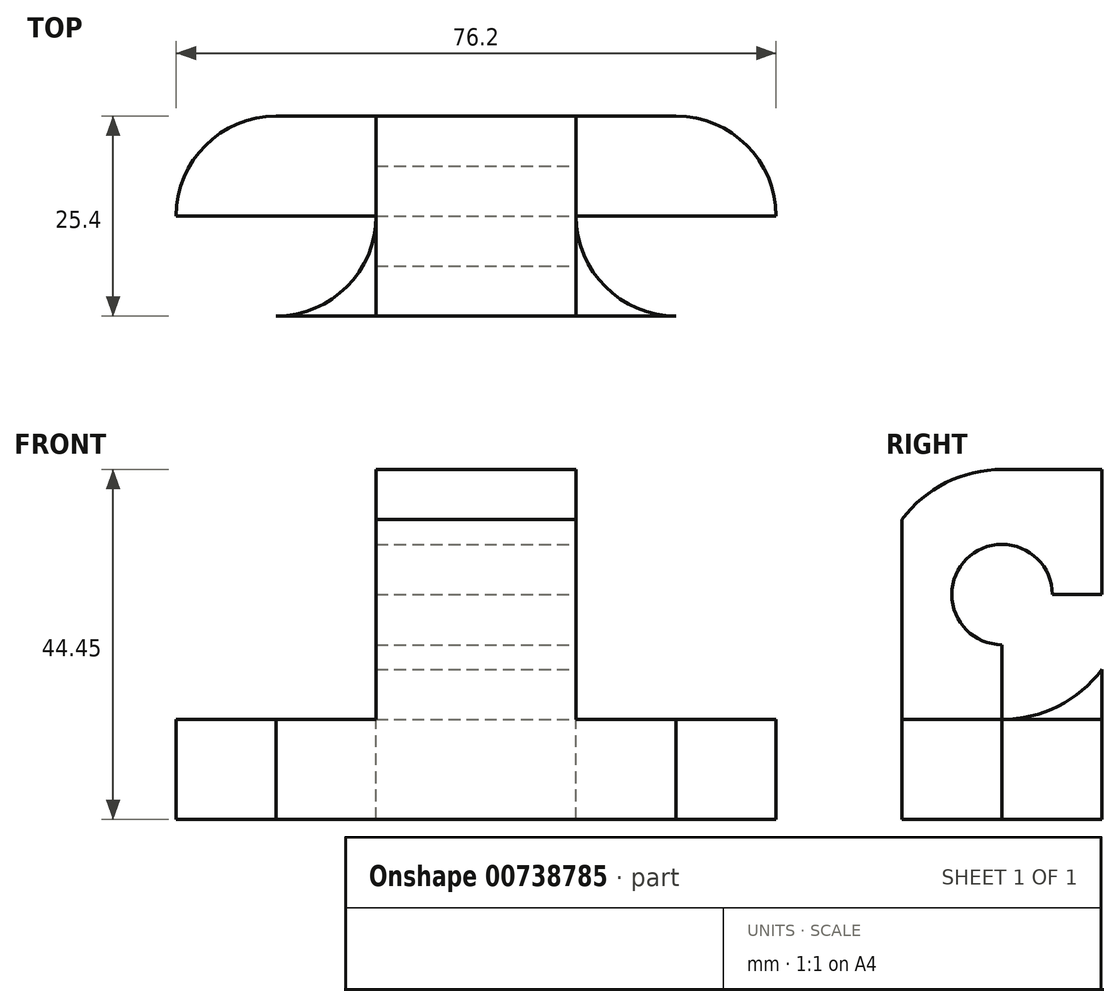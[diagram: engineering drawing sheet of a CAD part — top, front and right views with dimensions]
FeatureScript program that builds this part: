
annotation { "Feature Type Name" : "Feature", "Feature Type Description" : "" }
export const myFeature = defineFeature(function(context is Context, id is Id, definition is map)
    precondition{}
    {
        {
            var Q0;
            Q0=qCreatedBy(makeId("Front.planeOp"),FACE);
            var sketch = newSketch(context, id + "F0", { "sketchPlane" : qUnion([Q0])});
            skLineSegment(sketch, "E0", {"start": v(-25.4, 0) * mm, "end": v(-25.4, 12.7) * mm});
            skLineSegment(sketch, "E1", {"start": v(-25.4, 12.7) * mm, "end": v(0, 12.7) * mm});
            skLineSegment(sketch, "E2", {"start": v(0, 12.7) * mm, "end": v(0, 44.45) * mm});
            skLineSegment(sketch, "E3", {"start": v(0, 44.45) * mm, "end": v(25.4, 44.45) * mm});
            skLineSegment(sketch, "E4", {"start": v(25.4, 44.45) * mm, "end": v(25.4, 12.7) * mm});
            skLineSegment(sketch, "E5", {"start": v(25.4, 12.7) * mm, "end": v(50.8, 12.7) * mm});
            skLineSegment(sketch, "E6", {"start": v(50.8, 12.7) * mm, "end": v(50.8, 0) * mm});
            skLineSegment(sketch, "E7", {"start": v(50.8, 0) * mm, "end": v(-25.4, 0) * mm});
            skSolve(sketch);
        }
        {
            var Q0;
            Q0 = qSketchRegion(id + "F0", true);
            extrude(context, id + "F1", {"entities" : qUnion([Q0]), "depth" : 25.4 * mm, "offsetDistance" : 25.4 * mm});
        }
        {
            var Q0;
            Q0=makeQuery(id+"F1.opExtrude","SWEPT_FACE",FACE,{"disambiguationData":[OSD([sQuery(id+"F0.wireOp",EDGE,"E4")])]});
            var sketch = newSketch(context, id + "F2", { "sketchPlane" : qUnion([Q0])});
            skLineSegment(sketch, "E8", {"start": v(-12.7, 44.45) * mm, "end": v(-12.7, 12.7) * mm});
            skLineSegment(sketch, "E9", {"start": v(-25.4, 28.57) * mm, "end": v(0, 28.57) * mm});
            skCircle(sketch, "E10", {"center": v(-12.7, 28.57) * mm, "radius": 6.38 * mm});
            skCircle(sketch, "E11", {"center": v(-12.7, 28.57) * mm, "radius": 15.88 * mm});
            skSolve(sketch);
        }
        {
            var Q0;
            {var subQ0=sQuery(id+"F2.wireOp",EDGE,"E11");var subQ1=makeQuery(id+"F1.opExtrude","CAP_EDGE",EDGE,{"disambiguationData":[OSD([sQuery(id+"F0.wireOp",EDGE,"E4")])],"isStart":false});var subQ2=makeQuery(id+"F2.imprint","INTERSECT",VERTEX,{"disambiguationData":[OD(0.0)],"derivedFrom":[subQ1,subQ0]});Q0=makeQuery(id+"F2.imprint","IMPRINT",FACE,{"disambiguationData":[TD([[makeQuery(id+"F2.imprint","IMPRINT",EDGE,{"disambiguationData":[TD([[subQ2,-1.0]])],"derivedFrom":subQ0}),1.0]])]});}
            var Q1;
            {var subQ0=sQuery(id+"F2.wireOp",EDGE,"E11");var subQ1=makeQuery(id+"F1.opExtrude","CAP_EDGE",EDGE,{"disambiguationData":[OSD([sQuery(id+"F0.wireOp",EDGE,"E4")])],"isStart":true});var subQ2=makeQuery(id+"F2.imprint","INTERSECT",VERTEX,{"disambiguationData":[OD(0.0)],"derivedFrom":[subQ1,subQ0]});Q1=makeQuery(id+"F2.imprint","IMPRINT",FACE,{"disambiguationData":[TD([[makeQuery(id+"F2.imprint","IMPRINT",EDGE,{"disambiguationData":[TD([[subQ2,1.0]])],"derivedFrom":subQ0}),1.0]])]});}
            var Q2;
            {var subQ0=sQuery(id+"F2.wireOp",EDGE,"E11");var subQ1=sQuery(id+"F0.wireOp",EDGE,"E4");var subQ4=makeQuery(id+"F1.opExtrude","CAP_EDGE",EDGE,{"disambiguationData":[OSD([subQ1])],"isStart":true});var subQ5=makeQuery(id+"F2.imprint","INTERSECT",VERTEX,{"disambiguationData":[OD(0.0)],"derivedFrom":[subQ4,subQ0]});Q2=makeQuery(id+"F2.imprint","IMPRINT",FACE,{"disambiguationData":[TD([[makeQuery(id+"F2.imprint","IMPRINT",EDGE,{"disambiguationData":[TD([[subQ5,1.0]])],"derivedFrom":subQ4}),-1.0]])]});}
            var Q3;
            {var subQ0=sQuery(id+"F2.wireOp",EDGE,"E11");var subQ1=sQuery(id+"F0.wireOp",EDGE,"E4");var subQ4=makeQuery(id+"F1.opExtrude","CAP_EDGE",EDGE,{"disambiguationData":[OSD([subQ1])],"isStart":false});var subQ5=makeQuery(id+"F2.imprint","INTERSECT",VERTEX,{"disambiguationData":[OD(0.0)],"derivedFrom":[subQ4,subQ0]});Q3=makeQuery(id+"F2.imprint","IMPRINT",FACE,{"disambiguationData":[TD([[makeQuery(id+"F2.imprint","IMPRINT",EDGE,{"disambiguationData":[TD([[subQ5,1.0]])],"derivedFrom":subQ4}),1.0]])]});}
            var Q4;
            {var subQ0=sQuery(id+"F2.wireOp",EDGE,"E10");var subQ1=sQuery(id+"F2.wireOp",EDGE,"E8");var subQ2=makeQuery(id+"F2.imprint","INTERSECT",VERTEX,{"disambiguationData":[OD(0.0)],"derivedFrom":[subQ1,subQ0]});Q4=makeQuery(id+"F2.imprint","IMPRINT",FACE,{"disambiguationData":[TD([[makeQuery(id+"F2.imprint","IMPRINT",EDGE,{"disambiguationData":[TD([[subQ2,-1.0]])],"derivedFrom":subQ1}),1.0]])]});}
            var Q5;
            {var subQ0=sQuery(id+"F2.wireOp",EDGE,"E10");var subQ1=sQuery(id+"F2.wireOp",EDGE,"E8");var subQ2=makeQuery(id+"F2.imprint","INTERSECT",VERTEX,{"disambiguationData":[OD(0.0)],"derivedFrom":[subQ1,subQ0]});Q5=makeQuery(id+"F2.imprint","IMPRINT",FACE,{"disambiguationData":[TD([[makeQuery(id+"F2.imprint","IMPRINT",EDGE,{"disambiguationData":[TD([[subQ2,-1.0]])],"derivedFrom":subQ1}),-1.0]])]});}
            var Q6;
            {var subQ0=sQuery(id+"F2.wireOp",EDGE,"E9");var subQ1=sQuery(id+"F2.wireOp",EDGE,"E8");var subQ2=makeQuery(id+"F2.imprint","INTERSECT",VERTEX,{"derivedFrom":[subQ1,subQ0]});Q6=makeQuery(id+"F2.imprint","IMPRINT",FACE,{"disambiguationData":[TD([[makeQuery(id+"F2.imprint","IMPRINT",EDGE,{"disambiguationData":[TD([[subQ2,-1.0]])],"derivedFrom":subQ1}),1.0]])]});}
            var Q7;
            {var subQ0=sQuery(id+"F2.wireOp",EDGE,"E9");var subQ1=sQuery(id+"F2.wireOp",EDGE,"E8");var subQ2=makeQuery(id+"F2.imprint","INTERSECT",VERTEX,{"derivedFrom":[subQ1,subQ0]});Q7=makeQuery(id+"F2.imprint","IMPRINT",FACE,{"disambiguationData":[TD([[makeQuery(id+"F2.imprint","IMPRINT",EDGE,{"disambiguationData":[TD([[subQ2,-1.0]])],"derivedFrom":subQ1}),-1.0]])]});}
            extrude(context, id + "F3", {"entities" : qUnion([Q0, Q1, Q2, Q3, Q4, Q5, Q6, Q7]), "operationType" : NewBodyOperationType.REMOVE, "oppositeDirection" : true, "depth" : 25.4 * mm, "offsetDistance" : 25.4 * mm});
        }
        {
            var Q0;
            Q0=makeQuery(id+"F1.opExtrude","SWEPT_FACE",FACE,{"disambiguationData":[OSD([sQuery(id+"F0.wireOp",EDGE,"E5")])]});
            var sketch = newSketch(context, id + "F4", { "sketchPlane" : qUnion([Q0])});
            skLineSegment(sketch, "E12", {"start": v(38.1, 0) * mm, "end": v(38.1, -25.4) * mm});
            skLineSegment(sketch, "E13", {"start": v(50.8, -12.7) * mm, "end": v(25.4, -12.7) * mm});
            skCircle(sketch, "E14", {"center": v(38.1, -12.7) * mm, "radius": 6.35 * mm});
            skCircle(sketch, "E15", {"center": v(38.1, -12.7) * mm, "radius": 12.7 * mm});
            skSolve(sketch);
        }
        {
            var Q0;
            {var subQ0=sQuery(id+"F4.wireOp",EDGE,"E13");var subQ1=sQuery(id+"F4.wireOp",EDGE,"E12");var subQ2=makeQuery(id+"F4.imprint","INTERSECT",VERTEX,{"derivedFrom":[subQ1,subQ0]});Q0=makeQuery(id+"F4.imprint","IMPRINT",FACE,{"disambiguationData":[TD([[makeQuery(id+"F4.imprint","IMPRINT",EDGE,{"disambiguationData":[TD([[subQ2,-1.0]])],"derivedFrom":subQ1}),1.0]])]});}
            var Q1;
            {var subQ0=sQuery(id+"F4.wireOp",EDGE,"E14");var subQ1=sQuery(id+"F4.wireOp",EDGE,"E12");var subQ2=makeQuery(id+"F4.imprint","INTERSECT",VERTEX,{"disambiguationData":[OD(0.0)],"derivedFrom":[subQ1,subQ0]});Q1=makeQuery(id+"F4.imprint","IMPRINT",FACE,{"disambiguationData":[TD([[makeQuery(id+"F4.imprint","IMPRINT",EDGE,{"disambiguationData":[TD([[subQ2,-1.0]])],"derivedFrom":subQ1}),1.0]])]});}
            var Q2;
            {var subQ0=sQuery(id+"F4.wireOp",EDGE,"E14");var subQ1=sQuery(id+"F4.wireOp",EDGE,"E12");var subQ2=makeQuery(id+"F4.imprint","INTERSECT",VERTEX,{"disambiguationData":[OD(0.0)],"derivedFrom":[subQ1,subQ0]});Q2=makeQuery(id+"F4.imprint","IMPRINT",FACE,{"disambiguationData":[TD([[makeQuery(id+"F4.imprint","IMPRINT",EDGE,{"disambiguationData":[TD([[subQ2,-1.0]])],"derivedFrom":subQ1}),-1.0]])]});}
            var Q3;
            {var subQ0=sQuery(id+"F4.wireOp",EDGE,"E13");var subQ1=sQuery(id+"F4.wireOp",EDGE,"E12");var subQ2=makeQuery(id+"F4.imprint","INTERSECT",VERTEX,{"derivedFrom":[subQ1,subQ0]});Q3=makeQuery(id+"F4.imprint","IMPRINT",FACE,{"disambiguationData":[TD([[makeQuery(id+"F4.imprint","IMPRINT",EDGE,{"disambiguationData":[TD([[subQ2,-1.0]])],"derivedFrom":subQ1}),-1.0]])]});}
            var Q4;
            {var subQ1=sQuery(id+"F0.wireOp",EDGE,"E5");var subQ2=makeQuery(id+"F1.opExtrude","CAP_EDGE",EDGE,{"disambiguationData":[OSD([subQ1])],"isStart":true});var subQ4=makeQuery(id+"F1.opExtrude","SWEPT_EDGE",EDGE,{"disambiguationData":[OSD([subQ1,sQuery(id+"F0.wireOp",EDGE,"E6")])]});var subQ6=makeQuery(id+"F4.imprint","INTERSECT",VERTEX,{"derivedFrom":[subQ4,subQ2]});Q4=makeQuery(id+"F4.imprint","IMPRINT",FACE,{"disambiguationData":[TD([[makeQuery(id+"F4.imprint","IMPRINT",EDGE,{"disambiguationData":[TD([[subQ6,1.0]])],"derivedFrom":subQ2}),-1.0]])]});}
            var Q5;
            {var subQ1=sQuery(id+"F0.wireOp",EDGE,"E5");var subQ2=makeQuery(id+"F1.opExtrude","CAP_EDGE",EDGE,{"disambiguationData":[OSD([subQ1])],"isStart":false});var subQ4=makeQuery(id+"F1.opExtrude","SWEPT_EDGE",EDGE,{"disambiguationData":[OSD([subQ1,sQuery(id+"F0.wireOp",EDGE,"E6")])]});var subQ6=makeQuery(id+"F4.imprint","INTERSECT",VERTEX,{"derivedFrom":[subQ4,subQ2]});Q5=makeQuery(id+"F4.imprint","IMPRINT",FACE,{"disambiguationData":[TD([[makeQuery(id+"F4.imprint","IMPRINT",EDGE,{"disambiguationData":[TD([[subQ6,1.0]])],"derivedFrom":subQ2}),1.0]])]});}
            extrude(context, id + "F5", {"entities" : qUnion([Q0, Q1, Q2, Q3, Q4, Q5]), "operationType" : NewBodyOperationType.REMOVE, "oppositeDirection" : true, "depth" : 25.4 * mm, "offsetDistance" : 25.4 * mm});
        }
        {
            var Q0;
            Q0=makeQuery(id+"F1.opExtrude","SWEPT_FACE",FACE,{"disambiguationData":[OSD([sQuery(id+"F0.wireOp",EDGE,"E1")])]});
            var sketch = newSketch(context, id + "F6", { "sketchPlane" : qUnion([Q0])});
            skLineSegment(sketch, "E16", {"start": v(-12.7, 0) * mm, "end": v(-12.7, -25.4) * mm});
            skLineSegment(sketch, "E17", {"start": v(-25.4, -12.7) * mm, "end": v(0, -12.7) * mm});
            skCircle(sketch, "E18", {"center": v(-12.7, -12.7) * mm, "radius": 6.35 * mm});
            skCircle(sketch, "E19", {"center": v(-12.7, -12.7) * mm, "radius": 12.7 * mm});
            skSolve(sketch);
        }
        {
            var Q0;
            {var subQ0=sQuery(id+"F6.wireOp",EDGE,"E17");var subQ1=sQuery(id+"F6.wireOp",EDGE,"E16");var subQ2=makeQuery(id+"F6.imprint","INTERSECT",VERTEX,{"derivedFrom":[subQ1,subQ0]});Q0=makeQuery(id+"F6.imprint","IMPRINT",FACE,{"disambiguationData":[TD([[makeQuery(id+"F6.imprint","IMPRINT",EDGE,{"disambiguationData":[TD([[subQ2,-1.0]])],"derivedFrom":subQ1}),1.0]])]});}
            var Q1;
            {var subQ0=sQuery(id+"F6.wireOp",EDGE,"E17");var subQ1=sQuery(id+"F6.wireOp",EDGE,"E16");var subQ2=makeQuery(id+"F6.imprint","INTERSECT",VERTEX,{"derivedFrom":[subQ1,subQ0]});Q1=makeQuery(id+"F6.imprint","IMPRINT",FACE,{"disambiguationData":[TD([[makeQuery(id+"F6.imprint","IMPRINT",EDGE,{"disambiguationData":[TD([[subQ2,-1.0]])],"derivedFrom":subQ1}),-1.0]])]});}
            var Q2;
            {var subQ0=sQuery(id+"F6.wireOp",EDGE,"E18");var subQ1=sQuery(id+"F6.wireOp",EDGE,"E16");var subQ2=makeQuery(id+"F6.imprint","INTERSECT",VERTEX,{"disambiguationData":[OD(0.0)],"derivedFrom":[subQ1,subQ0]});Q2=makeQuery(id+"F6.imprint","IMPRINT",FACE,{"disambiguationData":[TD([[makeQuery(id+"F6.imprint","IMPRINT",EDGE,{"disambiguationData":[TD([[subQ2,-1.0]])],"derivedFrom":subQ1}),-1.0]])]});}
            var Q3;
            {var subQ0=sQuery(id+"F6.wireOp",EDGE,"E18");var subQ1=sQuery(id+"F6.wireOp",EDGE,"E16");var subQ2=makeQuery(id+"F6.imprint","INTERSECT",VERTEX,{"disambiguationData":[OD(0.0)],"derivedFrom":[subQ1,subQ0]});Q3=makeQuery(id+"F6.imprint","IMPRINT",FACE,{"disambiguationData":[TD([[makeQuery(id+"F6.imprint","IMPRINT",EDGE,{"disambiguationData":[TD([[subQ2,-1.0]])],"derivedFrom":subQ1}),1.0]])]});}
            var Q4;
            {var subQ1=sQuery(id+"F0.wireOp",EDGE,"E1");var subQ2=makeQuery(id+"F1.opExtrude","CAP_EDGE",EDGE,{"disambiguationData":[OSD([subQ1])],"isStart":false});var subQ4=makeQuery(id+"F1.opExtrude","SWEPT_EDGE",EDGE,{"disambiguationData":[OSD([sQuery(id+"F0.wireOp",EDGE,"E0"),subQ1])]});var subQ6=makeQuery(id+"F6.imprint","INTERSECT",VERTEX,{"derivedFrom":[subQ4,subQ2]});Q4=makeQuery(id+"F6.imprint","IMPRINT",FACE,{"disambiguationData":[TD([[makeQuery(id+"F6.imprint","IMPRINT",EDGE,{"disambiguationData":[TD([[subQ6,-1.0]])],"derivedFrom":subQ2}),1.0]])]});}
            var Q5;
            {var subQ1=sQuery(id+"F0.wireOp",EDGE,"E1");var subQ2=makeQuery(id+"F1.opExtrude","CAP_EDGE",EDGE,{"disambiguationData":[OSD([subQ1])],"isStart":true});var subQ4=makeQuery(id+"F1.opExtrude","SWEPT_EDGE",EDGE,{"disambiguationData":[OSD([sQuery(id+"F0.wireOp",EDGE,"E0"),subQ1])]});var subQ6=makeQuery(id+"F6.imprint","INTERSECT",VERTEX,{"derivedFrom":[subQ4,subQ2]});Q5=makeQuery(id+"F6.imprint","IMPRINT",FACE,{"disambiguationData":[TD([[makeQuery(id+"F6.imprint","IMPRINT",EDGE,{"disambiguationData":[TD([[subQ6,-1.0]])],"derivedFrom":subQ2}),-1.0]])]});}
            extrude(context, id + "F7", {"entities" : qUnion([Q0, Q1, Q2, Q3, Q4, Q5]), "operationType" : NewBodyOperationType.REMOVE, "oppositeDirection" : true, "depth" : 25.4 * mm, "offsetDistance" : 25.4 * mm});
        }
    });
